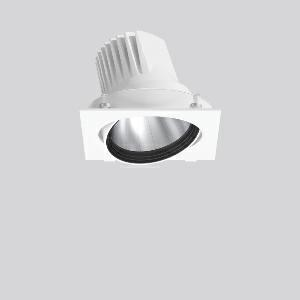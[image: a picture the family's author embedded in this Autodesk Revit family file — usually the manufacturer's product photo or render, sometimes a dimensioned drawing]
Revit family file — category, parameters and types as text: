
# Revit family: magcardo_maxi_722195_002_3_76_066e
name_source: partatom
category: Lighting Fixtures
units: mm (PartAtom-declared; Revit-internal decimal feet)

## family parameters
Cut with Voids When Loaded = No
Host = Face
Light Source = No
Part Type = Normal
Room Calculation Point = No
Round Connector Dimension = Use Diameter
Shared = No

## types (1)
- MAGCARDO maxi (1 x LED Modul 935, 4400 lm, 3500)
    Apparent Load = 35 VA
    Approval mark = CE
    CIE Flux Codes = 100 100 100 100 100
    Color Rendering = 92
    Color Temperature = 3500
    Default Elevation = 1800 mm
    Description = Series: MAGCARDO maxi
Projector unit for tool-free mounting in separate recessed frame. Luminaire top: die-cast aluminium, powder-coated. Rotation range 356° and swivel range ± 35°. Inner cover prevents view into the false ceiling. Black plastic ring and recessed LED to prevent glare from the side. Optical assembly with reflector made of MIRO-Silver with 98% total light reflection for outstanding efficiency - can be changed without tools. Best colour rendering index Ra>90. Magnetic click locking mechanism for quick and convenient installation without tools: insert the recessed frame (1, 2 or 3-lamp) with clamp fastener (no tools required), push the luminaire head with the base plate into the recessed frame and fix magnetically. Including separate LED converter with connecting cable 600 mm.High quality converter without flickering and stroboscopic effect. Through-wiring box (5 pole) available as accessory. The following accessories can be mounted without use of tools: interchangeable lenses, honeycomb louvre, clear and frosted diffusers, white interchangeable plastic ring.Modular design: recessed mounting frame must be ordered separately! 
Colour: traffic white, matt (RAL 9016)
Length: 172 mm
Width: 167 mm
Height: 137 mm
Recess height: 155 mm
Lamp: LED
Socket: without socket
Colour temperature: 3500K
Colour rendering index (CRI): 92
System power: 35 W
Rated luminous flux: 4400 lm
Luminous efficiency: 126 lm/W
Control gear: Converter, dimmable, DALI
Protection class: II
Type of protection: IP 20
    Height = 0 mm  [stored 0 ft]
    Lamp = 1 x LED Modul 935
    Lamp Light Flux = 4400 lm
    Lamp count = 1
    Length = 172 mm
    Lifetime = 50000 h
    Luminous efficacy = 126 lm/W
    Manufacturer = RZB
    ModVariant = No
    Model = 722195.002.3.76
    Mounting Place = Ceiling, Wall
    Mounting Type = Recessed
    Number of Poles = 1
    OnlyDefault = Yes
    Power Factor = 1
    Product Name = MAGCARDO maxi
    Product group = Recessed projectors
    ProductGroupID = 401
    Protection Class = Protection class II
    Protection Degree = IP 20
    RLX_Detail_Level = 1
    RLX_Emergency_Light_Flux = 0 lm
    RLX_Emergency_Type = 0
    RLX_Emergency_Type_DB = No
    RlxData = <blob elided: 39701 chars, md5=55d0ee48>
    Socket = socket
    Standby Power = 0 W
    System Light Flux = 4400 lm
    System Power = 35 W
    Type Comments = Product without accessories
    Type Image = 722045.002.jpg
    URL = http://relux.com
    VarID = ---
    Voltage = 230 V
    Voltage Range = 220-240 V
    Weight = 0.00 kg
    Width = 167 mm

note: [stored X ft] marks values corroborated as IEEE doubles in the binary element streams (Revit-internal decimal feet)

## geometry (parser evidence)
native form markers: Blend x4, Sweep x11
no freeform markers — native parametric forms only
